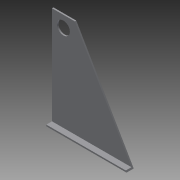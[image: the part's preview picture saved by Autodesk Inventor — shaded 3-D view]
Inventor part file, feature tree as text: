
AUTODESK INVENTOR PART (.ipt)
format: ipt  version: 2013 (Build 170138000, 138)  size: 94,208 bytes
history: native  units: in
note: dims shown in document units (in); Inventor stores cm internally (conversion verified against a paired STEP export)
features: extrude x3, sketch x3
ambient origin geometry x8: Origin, YZ Plane, XZ Plane, XY Plane, X Axis, Y Axis, Z Axis, Center Point
bodies: Solid1 (feature_tree)
feature tree (6):
  extrude  "Extrusion1"  Depth=8.688in
  extrude  "Extrusion2"  Depth=0.125in TaperAngle=0.0deg
  extrude  "Extrusion3"  Depth=0.5in TaperAngle=0.0deg
  sketch  "Sketch1"  dims[d0=2.0in d1=8.688in]
  sketch  "Sketch2"  dims[d2=60.0deg d3=0.125in d4=0.0in]
  sketch  "Sketch3"  dims[d5=0.125in d6=0.5in d7=0.0in d8=1.0in d9=1.0in d10=1.125in d11=1.0in d12=0.0in]
